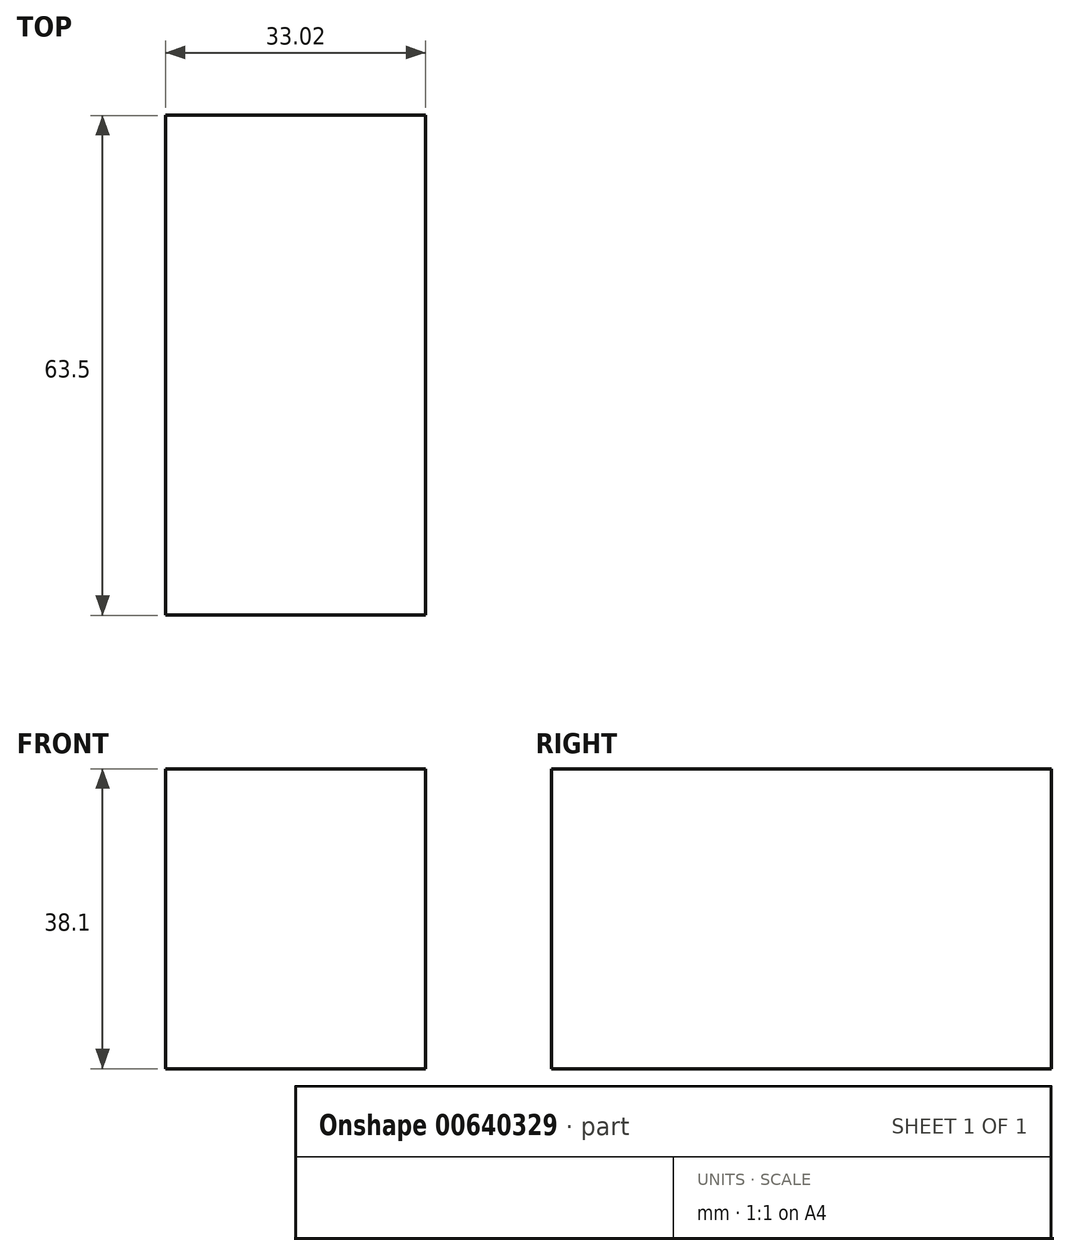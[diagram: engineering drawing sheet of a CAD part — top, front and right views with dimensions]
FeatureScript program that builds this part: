
annotation { "Feature Type Name" : "Feature", "Feature Type Description" : "" }
export const myFeature = defineFeature(function(context is Context, id is Id, definition is map)
    precondition{}
    {
        {
            var Q0;
            Q0=qCreatedBy(makeId("Top.planeOp"),FACE);
            var sketch = newSketch(context, id + "F0", { "sketchPlane" : qUnion([Q0])});
            skLineSegment(sketch, "E0.bottom", {"start": v(-26.56, 26.04) * mm, "end": v(6.46, 26.04) * mm});
            skLineSegment(sketch, "E0.top", {"start": v(-26.56, -37.46) * mm, "end": v(6.46, -37.46) * mm});
            skLineSegment(sketch, "E0.left", {"start": v(-26.56, 26.04) * mm, "end": v(-26.56, -37.46) * mm});
            skLineSegment(sketch, "E0.right", {"start": v(6.46, 26.04) * mm, "end": v(6.46, -37.46) * mm});
            skSolve(sketch);
        }
        {
            var Q0;
            Q0=makeQuery(id+"F0.imprint","IMPRINT",FACE,{"disambiguationData":[TD([[makeQuery(id+"F0.imprint","IMPRINT",EDGE,{"derivedFrom":sQuery(id+"F0.wireOp",EDGE,"E0.bottom")}),-1.0]])]});
            extrude(context, id + "F1", {"entities" : qUnion([Q0]), "depth" : 38.1 * mm, "offsetDistance" : 25.4 * mm});
        }
    });
